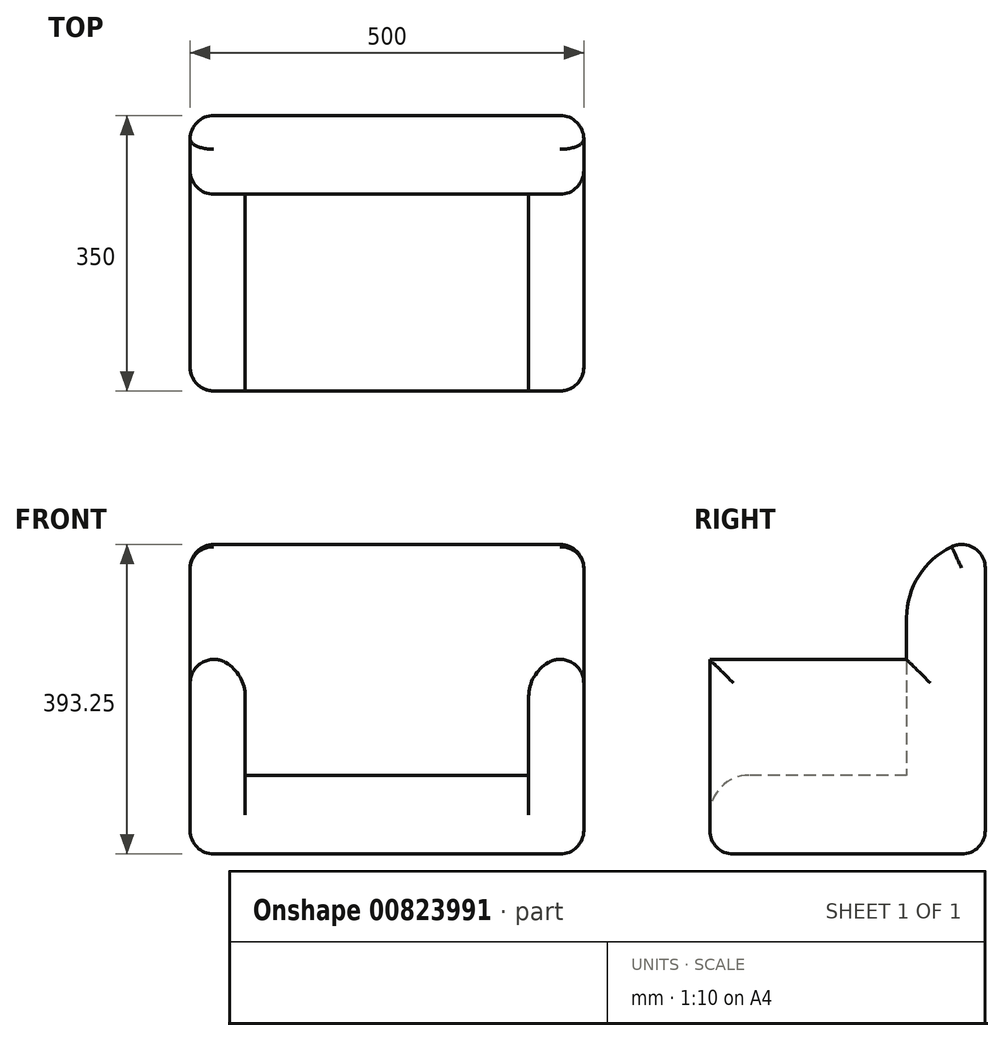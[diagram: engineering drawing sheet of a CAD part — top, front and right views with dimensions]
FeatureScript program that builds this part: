
annotation { "Feature Type Name" : "Feature", "Feature Type Description" : "" }
export const myFeature = defineFeature(function(context is Context, id is Id, definition is map)
    precondition{}
    {
        {
            var Q0;
            Q0=qCreatedBy(makeId("Top.planeOp"),FACE);
            var sketch = newSketch(context, id + "F0", { "sketchPlane" : qUnion([Q0])});
            skLineSegment(sketch, "E0.bottom", {"start": v(-250, 175) * mm, "end": v(250, 175) * mm});
            skLineSegment(sketch, "E0.top", {"start": v(-250, -175) * mm, "end": v(250, -175) * mm});
            skLineSegment(sketch, "E0.left", {"start": v(-250, 175) * mm, "end": v(-250, -175) * mm});
            skLineSegment(sketch, "E0.right", {"start": v(250, 175) * mm, "end": v(250, -175) * mm});
            skSolve(sketch);
        }
        {
            var Q0;
            Q0=makeQuery(id+"F0.imprint","IMPRINT",FACE,{"disambiguationData":[TD([[makeQuery(id+"F0.imprint","IMPRINT",EDGE,{"derivedFrom":sQuery(id+"F0.wireOp",EDGE,"E0.bottom")}),-1.0]])]});
            extrude(context, id + "F1", {"entities" : qUnion([Q0]), "depth" : 100 * mm, "offsetDistance" : 25 * mm});
        }
        {
            var Q0;
            Q0=makeQuery(id+"F1.opExtrude","CAP_FACE",FACE,{"disambiguationData":[OSD([sQuery(id+"F0.wireOp",EDGE,"E0.bottom"),sQuery(id+"F0.wireOp",EDGE,"E0.top"),sQuery(id+"F0.wireOp",EDGE,"E0.left"),sQuery(id+"F0.wireOp",EDGE,"E0.right")])],"isStart":false});
            var sketch = newSketch(context, id + "F2", { "sketchPlane" : qUnion([Q0])});
            skLineSegment(sketch, "E1.bottom", {"start": v(-250, 175) * mm, "end": v(250, 175) * mm});
            skLineSegment(sketch, "E1.top", {"start": v(-250, 75) * mm, "end": v(250, 75) * mm});
            skLineSegment(sketch, "E1.left", {"start": v(-250, 175) * mm, "end": v(-250, 75) * mm});
            skLineSegment(sketch, "E1.right", {"start": v(250, 175) * mm, "end": v(250, 75) * mm});
            skSolve(sketch);
        }
        {
            var Q0;
            Q0=makeQuery(id+"F2.imprint","IMPRINT",FACE,{"disambiguationData":[TD([[makeQuery(id+"F2.imprint","IMPRINT",EDGE,{"derivedFrom":sQuery(id+"F2.wireOp",EDGE,"E1.bottom")}),-1.0]])]});
            extrude(context, id + "F3", {"entities" : qUnion([Q0]), "operationType" : NewBodyOperationType.ADD, "depth" : 300 * mm, "offsetDistance" : 25 * mm});
        }
        {
            var Q0;
            Q0=makeQuery(id+"F1.opExtrude","CAP_FACE",FACE,{"disambiguationData":[OSD([sQuery(id+"F0.wireOp",EDGE,"E0.bottom"),sQuery(id+"F0.wireOp",EDGE,"E0.top"),sQuery(id+"F0.wireOp",EDGE,"E0.left"),sQuery(id+"F0.wireOp",EDGE,"E0.right")])],"isStart":false});
            var sketch = newSketch(context, id + "F4", { "sketchPlane" : qUnion([Q0])});
            skLineSegment(sketch, "E2.bottom", {"start": v(250, 75) * mm, "end": v(180, 75) * mm});
            skLineSegment(sketch, "E2.top", {"start": v(250, -175) * mm, "end": v(180, -175) * mm});
            skLineSegment(sketch, "E2.left", {"start": v(250, 75) * mm, "end": v(250, -175) * mm});
            skLineSegment(sketch, "E2.right", {"start": v(180, 75) * mm, "end": v(180, -175) * mm});
            skLineSegment(sketch, "E3.bottom", {"start": v(-180, 75) * mm, "end": v(-250, 75) * mm});
            skLineSegment(sketch, "E3.top", {"start": v(-180, -175) * mm, "end": v(-250, -175) * mm});
            skLineSegment(sketch, "E3.left", {"start": v(-180, 75) * mm, "end": v(-180, -175) * mm});
            skLineSegment(sketch, "E3.right", {"start": v(-250, 75) * mm, "end": v(-250, -175) * mm});
            skSolve(sketch);
        }
        {
            var Q0;
            Q0=makeQuery(id+"F4.imprint","IMPRINT",FACE,{"disambiguationData":[TD([[makeQuery(id+"F4.imprint","IMPRINT",EDGE,{"derivedFrom":sQuery(id+"F4.wireOp",EDGE,"E2.bottom")}),-1.0]])]});
            var Q1;
            Q1=makeQuery(id+"F4.imprint","IMPRINT",FACE,{"disambiguationData":[TD([[makeQuery(id+"F4.imprint","IMPRINT",EDGE,{"derivedFrom":sQuery(id+"F4.wireOp",EDGE,"E3.bottom")}),-1.0]])]});
            extrude(context, id + "F5", {"entities" : qUnion([Q0, Q1]), "operationType" : NewBodyOperationType.ADD, "depth" : 150 * mm, "offsetDistance" : 25 * mm});
        }
        {
            var Q0;
            Q0=makeQuery(id+"F3.opExtrude","CAP_EDGE",EDGE,{"disambiguationData":[OSD([sQuery(id+"F2.wireOp",EDGE,"E1.top")])],"isStart":false});
            fillet(context, id + "F6", {"entities" : qUnion([Q0]), "radius" : 100 * mm, "tangentPropagation" : true, "allowEdgeOverflow" : false});
        }
        {
            var Q0;
            Q0=makeQuery(id+"F5.opExtrude","CAP_EDGE",EDGE,{"disambiguationData":[OSD([sQuery(id+"F4.wireOp",EDGE,"E3.left")])],"isStart":false});
            var Q1;
            Q1=makeQuery(id+"F5.opExtrude","CAP_EDGE",EDGE,{"disambiguationData":[OSD([sQuery(id+"F4.wireOp",EDGE,"E2.right")])],"isStart":false});
            var Q2;
            Q2=makeQuery(id+"F5.opExtrude","CAP_EDGE",EDGE,{"disambiguationData":[OSD([sQuery(id+"F4.wireOp",EDGE,"E3.left")])],"isStart":true});
            var Q3;
            Q3=makeQuery(id+"F3.opExtrude","CAP_EDGE",EDGE,{"disambiguationData":[OSD([sQuery(id+"F2.wireOp",EDGE,"E1.top")])],"isStart":true});
            var Q4;
            Q4=makeQuery(id+"F5.opExtrude","CAP_EDGE",EDGE,{"disambiguationData":[OSD([sQuery(id+"F4.wireOp",EDGE,"E2.right")])],"isStart":true});
            var Q5;
            Q5=makeQuery(id+"F1.opExtrude","CAP_EDGE",EDGE,{"disambiguationData":[OSD([sQuery(id+"F0.wireOp",EDGE,"E0.top")])],"isStart":false});
            fillet(context, id + "F7", {"entities" : qUnion([Q0, Q1, Q2, Q3, Q4, Q5]), "radius" : 50 * mm, "tangentPropagation" : true, "allowEdgeOverflow" : false});
        }
        {
            var Q0;
            Q0=makeQuery(id+"F5.opExtrude","CAP_EDGE",EDGE,{"disambiguationData":[OSD([sQuery(id+"F4.wireOp",EDGE,"E3.right")])],"isStart":false});
            var Q1;
            Q1=makeQuery(id+"F3.boolean.opBoolean","MERGE",EDGE,{"derivedFrom":[makeQuery(id+"F1.opExtrude","SWEPT_EDGE",EDGE,{"disambiguationData":[OSD([sQuery(id+"F0.wireOp",EDGE,"E0.bottom"),sQuery(id+"F0.wireOp",EDGE,"E0.left")])]}),makeQuery(id+"F3.opExtrude","SWEPT_EDGE",EDGE,{"disambiguationData":[OSD([sQuery(id+"F2.wireOp",EDGE,"E1.bottom"),sQuery(id+"F2.wireOp",EDGE,"E1.left")])]})]});
            var Q2;
            Q2=makeQuery(id+"F5.opExtrude","CAP_EDGE",EDGE,{"disambiguationData":[OSD([sQuery(id+"F4.wireOp",EDGE,"E2.left")])],"isStart":false});
            var Q3;
            Q3=makeQuery(id+"F6.opFillet","BLEND_EDGE",EDGE,{"blendedFrom":[makeQuery(id+"F3.opExtrude","CAP_EDGE",EDGE,{"disambiguationData":[OSD([sQuery(id+"F2.wireOp",EDGE,"E1.top")])],"isStart":false}),makeQuery(id+"F5.boolean.opBoolean","MERGE",FACE,{"derivedFrom":[makeQuery(id+"F3.boolean.opBoolean","MERGE",FACE,{"derivedFrom":[makeQuery(id+"F1.opExtrude","SWEPT_FACE",FACE,{"disambiguationData":[OSD([sQuery(id+"F0.wireOp",EDGE,"E0.right")])]}),makeQuery(id+"F3.opExtrude","SWEPT_FACE",FACE,{"disambiguationData":[OSD([sQuery(id+"F2.wireOp",EDGE,"E1.right")])]})]}),makeQuery(id+"F5.opExtrude","SWEPT_FACE",FACE,{"disambiguationData":[OSD([sQuery(id+"F4.wireOp",EDGE,"E2.left")])]})]})],"blendedInto":[makeQuery(id+"F5.boolean.opBoolean","MERGE",FACE,{"derivedFrom":[makeQuery(id+"F3.boolean.opBoolean","MERGE",FACE,{"derivedFrom":[makeQuery(id+"F1.opExtrude","SWEPT_FACE",FACE,{"disambiguationData":[OSD([sQuery(id+"F0.wireOp",EDGE,"E0.right")])]}),makeQuery(id+"F3.opExtrude","SWEPT_FACE",FACE,{"disambiguationData":[OSD([sQuery(id+"F2.wireOp",EDGE,"E1.right")])]})]}),makeQuery(id+"F5.opExtrude","SWEPT_FACE",FACE,{"disambiguationData":[OSD([sQuery(id+"F4.wireOp",EDGE,"E2.left")])]})]})]});
            var Q4;
            Q4=makeQuery(id+"F6.opFillet","BLEND_EDGE",EDGE,{"blendedFrom":[makeQuery(id+"F3.opExtrude","CAP_EDGE",EDGE,{"disambiguationData":[OSD([sQuery(id+"F2.wireOp",EDGE,"E1.top")])],"isStart":false}),makeQuery(id+"F5.boolean.opBoolean","MERGE",FACE,{"derivedFrom":[makeQuery(id+"F3.boolean.opBoolean","MERGE",FACE,{"derivedFrom":[makeQuery(id+"F1.opExtrude","SWEPT_FACE",FACE,{"disambiguationData":[OSD([sQuery(id+"F0.wireOp",EDGE,"E0.left")])]}),makeQuery(id+"F3.opExtrude","SWEPT_FACE",FACE,{"disambiguationData":[OSD([sQuery(id+"F2.wireOp",EDGE,"E1.left")])]})]}),makeQuery(id+"F5.opExtrude","SWEPT_FACE",FACE,{"disambiguationData":[OSD([sQuery(id+"F4.wireOp",EDGE,"E3.right")])]})]})],"blendedInto":[makeQuery(id+"F5.boolean.opBoolean","MERGE",FACE,{"derivedFrom":[makeQuery(id+"F3.boolean.opBoolean","MERGE",FACE,{"derivedFrom":[makeQuery(id+"F1.opExtrude","SWEPT_FACE",FACE,{"disambiguationData":[OSD([sQuery(id+"F0.wireOp",EDGE,"E0.left")])]}),makeQuery(id+"F3.opExtrude","SWEPT_FACE",FACE,{"disambiguationData":[OSD([sQuery(id+"F2.wireOp",EDGE,"E1.left")])]})]}),makeQuery(id+"F5.opExtrude","SWEPT_FACE",FACE,{"disambiguationData":[OSD([sQuery(id+"F4.wireOp",EDGE,"E3.right")])]})]})]});
            var Q5;
            Q5=makeQuery(id+"F3.boolean.opBoolean","MERGE",EDGE,{"derivedFrom":[makeQuery(id+"F1.opExtrude","SWEPT_EDGE",EDGE,{"disambiguationData":[OSD([sQuery(id+"F0.wireOp",EDGE,"E0.bottom"),sQuery(id+"F0.wireOp",EDGE,"E0.right")])]}),makeQuery(id+"F3.opExtrude","SWEPT_EDGE",EDGE,{"disambiguationData":[OSD([sQuery(id+"F2.wireOp",EDGE,"E1.bottom"),sQuery(id+"F2.wireOp",EDGE,"E1.right")])]})]});
            var Q6;
            Q6=makeQuery(id+"F1.opExtrude","CAP_EDGE",EDGE,{"disambiguationData":[OSD([sQuery(id+"F0.wireOp",EDGE,"E0.right")])],"isStart":true});
            var Q7;
            Q7=makeQuery(id+"F1.opExtrude","CAP_EDGE",EDGE,{"disambiguationData":[OSD([sQuery(id+"F0.wireOp",EDGE,"E0.bottom")])],"isStart":true});
            var Q8;
            Q8=makeQuery(id+"F1.opExtrude","CAP_EDGE",EDGE,{"disambiguationData":[OSD([sQuery(id+"F0.wireOp",EDGE,"E0.left")])],"isStart":true});
            var Q9;
            Q9=makeQuery(id+"F5.boolean.opBoolean","MERGE",EDGE,{"derivedFrom":[makeQuery(id+"F1.opExtrude","SWEPT_EDGE",EDGE,{"disambiguationData":[OSD([sQuery(id+"F0.wireOp",EDGE,"E0.top"),sQuery(id+"F0.wireOp",EDGE,"E0.left")])]}),makeQuery(id+"F5.opExtrude","SWEPT_EDGE",EDGE,{"disambiguationData":[OSD([sQuery(id+"F4.wireOp",EDGE,"E3.top"),sQuery(id+"F4.wireOp",EDGE,"E3.right")])]})]});
            var Q10;
            Q10=makeQuery(id+"F5.boolean.opBoolean","MERGE",EDGE,{"derivedFrom":[makeQuery(id+"F1.opExtrude","SWEPT_EDGE",EDGE,{"disambiguationData":[OSD([sQuery(id+"F0.wireOp",EDGE,"E0.top"),sQuery(id+"F0.wireOp",EDGE,"E0.right")])]}),makeQuery(id+"F5.opExtrude","SWEPT_EDGE",EDGE,{"disambiguationData":[OSD([sQuery(id+"F4.wireOp",EDGE,"E2.top"),sQuery(id+"F4.wireOp",EDGE,"E2.left")])]})]});
            var Q11;
            Q11=makeQuery(id+"F1.opExtrude","CAP_EDGE",EDGE,{"disambiguationData":[OSD([sQuery(id+"F0.wireOp",EDGE,"E0.top")])],"isStart":true});
            fillet(context, id + "F8", {"entities" : qUnion([Q0, Q1, Q2, Q3, Q4, Q5, Q6, Q7, Q8, Q9, Q10, Q11]), "radius" : 30 * mm, "tangentPropagation" : true, "allowEdgeOverflow" : false});
        }
        {
            var Q0;
            Q0=makeQuery(id+"F6.opFillet","BLEND_EDGE",EDGE,{"blendedFrom":[makeQuery(id+"F3.opExtrude","CAP_EDGE",EDGE,{"disambiguationData":[OSD([sQuery(id+"F2.wireOp",EDGE,"E1.top")])],"isStart":false}),makeQuery(id+"F3.boolean.opBoolean","MERGE",FACE,{"derivedFrom":[makeQuery(id+"F1.opExtrude","SWEPT_FACE",FACE,{"disambiguationData":[OSD([sQuery(id+"F0.wireOp",EDGE,"E0.bottom")])]}),makeQuery(id+"F3.opExtrude","SWEPT_FACE",FACE,{"disambiguationData":[OSD([sQuery(id+"F2.wireOp",EDGE,"E1.bottom")])]})]})],"blendedInto":[makeQuery(id+"F3.boolean.opBoolean","MERGE",FACE,{"derivedFrom":[makeQuery(id+"F1.opExtrude","SWEPT_FACE",FACE,{"disambiguationData":[OSD([sQuery(id+"F0.wireOp",EDGE,"E0.bottom")])]}),makeQuery(id+"F3.opExtrude","SWEPT_FACE",FACE,{"disambiguationData":[OSD([sQuery(id+"F2.wireOp",EDGE,"E1.bottom")])]})]})]});
            fillet(context, id + "F9", {"entities" : qUnion([Q0]), "radius" : 30 * mm, "tangentPropagation" : true, "allowEdgeOverflow" : false});
        }
    });
